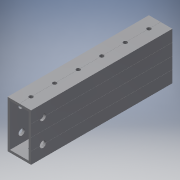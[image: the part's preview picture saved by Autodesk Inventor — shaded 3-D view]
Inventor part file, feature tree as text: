
AUTODESK INVENTOR PART (.ipt)
format: ipt  version: 2017 (Build 210142000, 142)  size: 253,440 bytes
history: native  units: in
note: dims shown in document units (in); Inventor stores cm internally (conversion verified against a paired STEP export)
features: other x3, sketch x1
ambient origin geometry x8: Origin, YZ Plane, XZ Plane, XY Plane, X Axis, Y Axis, Z Axis, Center Point
bodies: Solid1 (feature_tree)
feature tree (4):
  other  "VersaFrame_Short_End.ipt"
  other  "Solid1::VersaFrame_Short_End.ipt"
  other  "TaggingFeature1"
  sketch  "Sketch1"  dims[d0=0.3937in]
